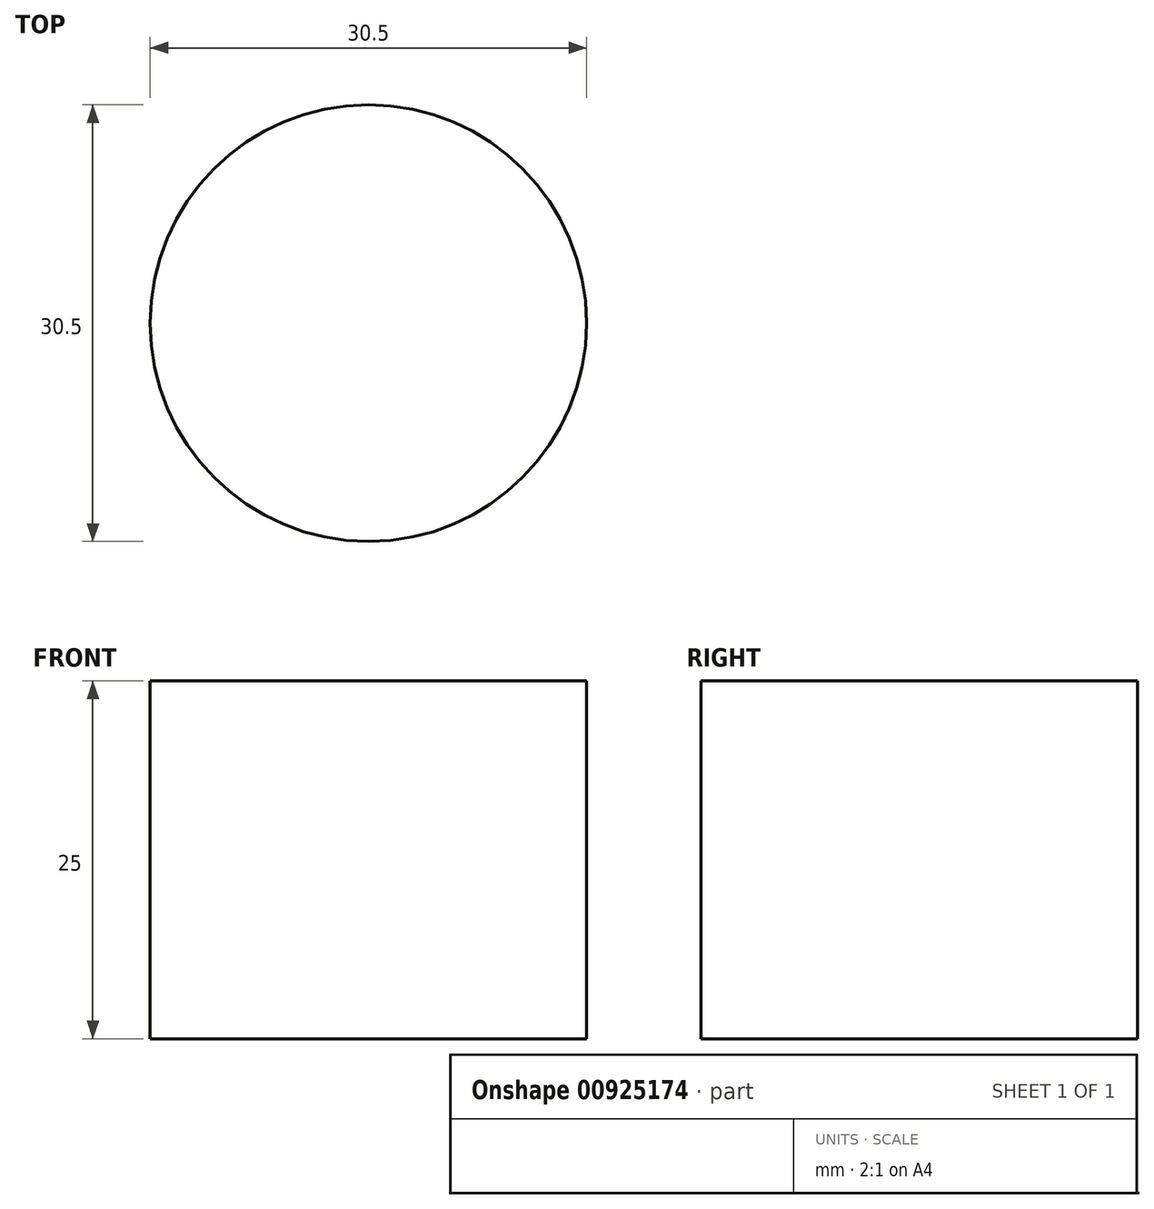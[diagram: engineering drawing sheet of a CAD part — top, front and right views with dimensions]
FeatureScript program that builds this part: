
annotation { "Feature Type Name" : "Feature", "Feature Type Description" : "" }
export const myFeature = defineFeature(function(context is Context, id is Id, definition is map)
    precondition{}
    {
        {
            var Q0;
            Q0=qCreatedBy(makeId("Top.planeOp"),FACE);
            var sketch = newSketch(context, id + "F0", { "sketchPlane" : qUnion([Q0])});
            skCircle(sketch, "E0", {"center": v(0, 0) * mm, "radius": 15.25 * mm});
            skSolve(sketch);
        }
        {
            var Q0;
            Q0 = qSketchRegion(id + "F0", true);
            extrude(context, id + "F1", {"entities" : qUnion([Q0]), "depth" : 25 * mm, "offsetDistance" : 25 * mm});
        }
    });
